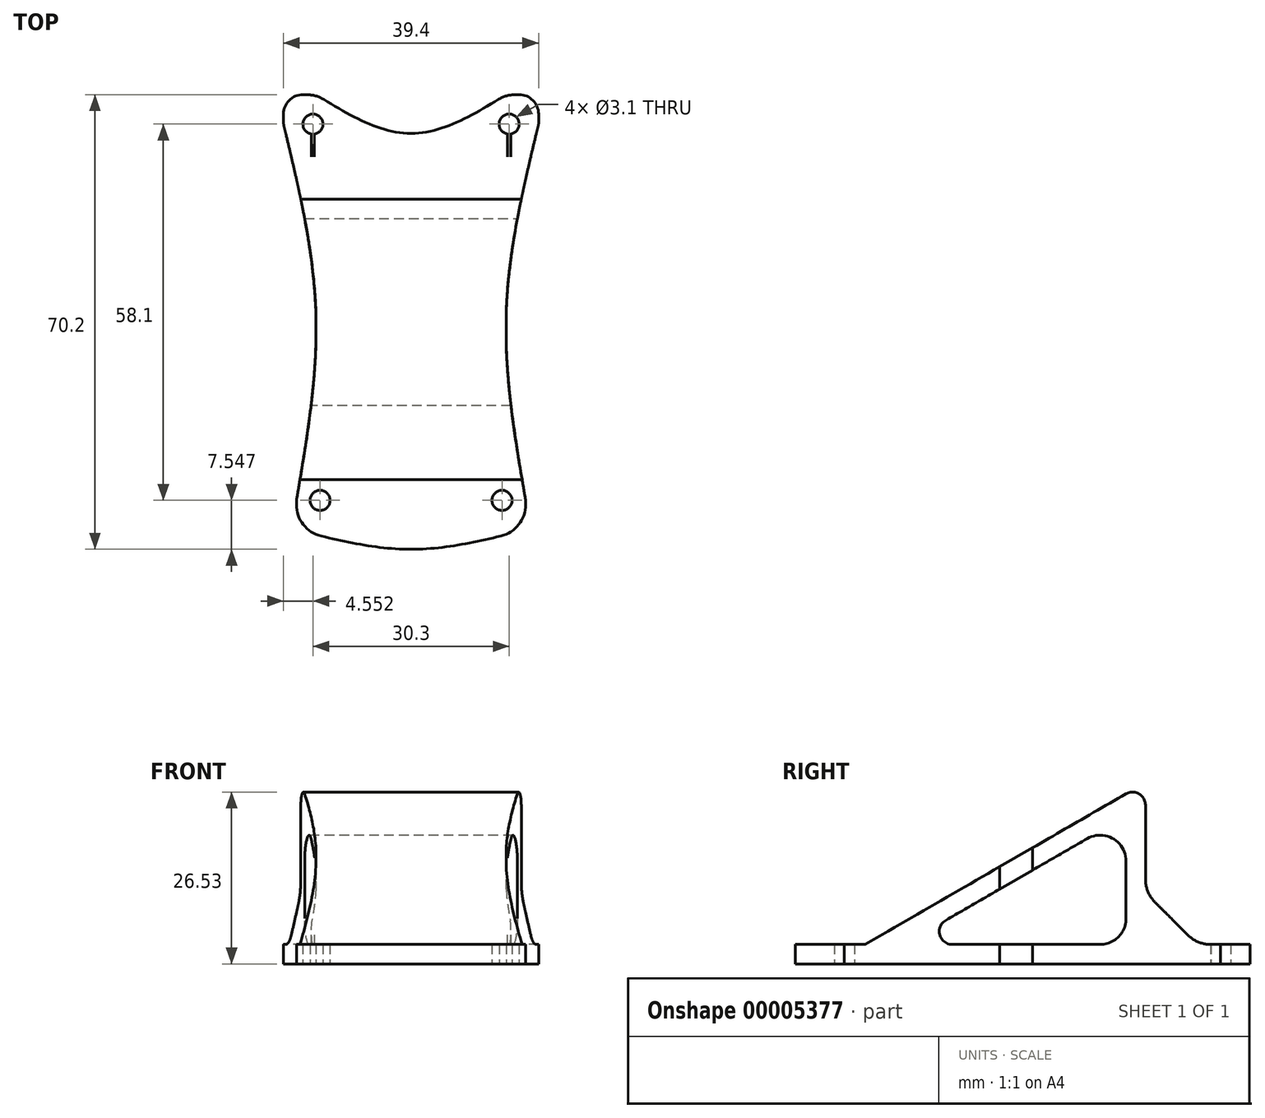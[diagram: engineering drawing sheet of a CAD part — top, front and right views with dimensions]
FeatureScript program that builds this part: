
annotation { "Feature Type Name" : "Feature", "Feature Type Description" : "" }
export const myFeature = defineFeature(function(context is Context, id is Id, definition is map)
    precondition{}
    {
        {
            var Q0;
            Q0=qCreatedBy(makeId("Top.planeOp"),FACE);
            var sketch = newSketch(context, id + "F0", { "sketchPlane" : qUnion([Q0])});
            skCircle(sketch, "E0", {"center": v(-54.15, 55.54) * mm, "radius": 1.55 * mm});
            skCircle(sketch, "E1", {"center": v(-23.85, 55.54) * mm, "radius": 1.55 * mm});
            skLineSegment(sketch, "E2.bottom", {"start": v(-58.7, 60.09) * mm, "end": v(-19.3, 60.09) * mm});
            skLineSegment(sketch, "E2.top", {"start": v(-58.7, -7.11) * mm, "end": v(-19.3, -7.11) * mm});
            skLineSegment(sketch, "E2.left", {"start": v(-58.7, 60.09) * mm, "end": v(-58.7, -7.11) * mm});
            skLineSegment(sketch, "E2.right", {"start": v(-19.3, 60.09) * mm, "end": v(-19.3, -7.11) * mm});
            skLineSegment(sketch, "E3", {"start": v(-19.3, 26.49) * mm, "end": v(-58.7, 26.49) * mm});
            skLineSegment(sketch, "E4", {"start": v(-39, 60.09) * mm, "end": v(-39, -7.11) * mm});
            skCircle(sketch, "E5", {"center": v(-24.95, -2.56) * mm, "radius": 1.55 * mm});
            skCircle(sketch, "E6", {"center": v(-53.05, -2.56) * mm, "radius": 1.55 * mm});
            skLineSegment(sketch, "E7", {"start": v(-56.7, -7.11) * mm, "end": v(-56.7, 60.09) * mm});
            skLineSegment(sketch, "E8", {"start": v(-53.7, 60.09) * mm, "end": v(-53.7, -7.11) * mm});
            skFitSpline(sketch, "E9", {"points": [v(-58.7, 55.54) * mm, v(-53.7, 26.49) * mm, v(-56.7, -2.56) * mm], "startDerivative": vector(13.98, -57.9) * mm, "endDerivative": vector(-10, -58.3) * mm});
            skLineSegment(sketch, "E10", {"start": v(-21.3, 60.09) * mm, "end": v(-21.3, -7.11) * mm});
            skLineSegment(sketch, "E11", {"start": v(-24.3, -7.11) * mm, "end": v(-24.3, 60.09) * mm});
            skFitSpline(sketch, "E12", {"points": [v(-19.3, 55.54) * mm, v(-24.3, 26.49) * mm, v(-21.3, -2.56) * mm], "startDerivative": vector(-13.98, -57.9) * mm, "endDerivative": vector(10, -58.3) * mm});
            skLineSegment(sketch, "E13", {"start": v(-58.7, -10.11) * mm, "end": v(-19.3, -10.11) * mm});
            skFitSpline(sketch, "E14", {"points": [v(-56.7, -7.11) * mm, v(-39, -10.11) * mm, v(-21.3, -7.11) * mm], "startDerivative": vector(35.4, -9) * mm, "endDerivative": vector(35.4, 9) * mm});
            skLineSegment(sketch, "E15", {"start": v(-44.39, 54.09) * mm, "end": v(-33.64, 54.09) * mm});
            skFitSpline(sketch, "E16", {"points": [v(-53.7, 60.09) * mm, v(-39, 54.09) * mm, v(-24.3, 60.09) * mm], "startDerivative": vector(29.4, -18) * mm, "endDerivative": vector(29.4, 18) * mm});
            skSolve(sketch);
        }
        {
            var Q0;
            Q0=makeQuery(id+"F0.imprint","IMPRINT",FACE,{"disambiguationData":[TD([[makeQuery(id+"F0.imprint","IMPRINT",EDGE,{"derivedFrom":sQuery(id+"F0.wireOp",EDGE,"E0")}),-1.0]])]});
            var Q1;
            Q1=makeQuery(id+"F0.imprint","IMPRINT",FACE,{"disambiguationData":[TD([[makeQuery(id+"F0.imprint","IMPRINT",EDGE,{"derivedFrom":sQuery(id+"F0.wireOp",EDGE,"E1")}),-1.0]])]});
            var Q2;
            Q2=makeQuery(id+"F0.imprint","IMPRINT",FACE,{"disambiguationData":[TD([[makeQuery(id+"F0.imprint","IMPRINT",EDGE,{"derivedFrom":sQuery(id+"F0.wireOp",EDGE,"e01dfe83-0717-4ae6-a988-163f855d4e40")}),-1.0]])]});
            var Q3;
            Q3=makeQuery(id+"F0.imprint","IMPRINT",FACE,{"disambiguationData":[TD([[makeQuery(id+"F0.imprint","IMPRINT",EDGE,{"derivedFrom":sQuery(id+"F0.wireOp",EDGE,"7627a010-1d8e-4650-84d9-1653207d3903")}),-1.0]])]});
            var Q4;
            {var subQ0=sQuery(id+"F0.wireOp",EDGE,"8a834bad-6aca-40db-864a-f019d0ae7b1d");Q4=makeQuery(id+"F0.imprint","IMPRINT",FACE,{"disambiguationData":[TD([[makeQuery(id+"F0.imprint","IMPRINT",EDGE,{"derivedFrom":subQ0}),1.0]])]});}
            var Q5;
            {var subQ7=sQuery(id+"F0.wireOp",EDGE,"E2.top");var subQ10=sQuery(id+"F0.wireOp",EDGE,"E4");var subQ12=makeQuery(id+"F0.imprint","INTERSECT",VERTEX,{"derivedFrom":[subQ7,subQ10]});Q5=makeQuery(id+"F0.imprint","IMPRINT",FACE,{"disambiguationData":[TD([[makeQuery(id+"F0.imprint","IMPRINT",EDGE,{"disambiguationData":[TD([[subQ12,1.0]])],"derivedFrom":subQ7}),1.0]])]});}
            var Q6;
            {var subQ1=sQuery(id+"F0.wireOp",EDGE,"E8");var subQ7=sQuery(id+"F0.wireOp",EDGE,"E0");var subQ8=makeQuery(id+"F0.imprint","INTERSECT",VERTEX,{"disambiguationData":[OD(0.0)],"derivedFrom":[subQ7,subQ1]});Q6=makeQuery(id+"F0.imprint","IMPRINT",FACE,{"disambiguationData":[TD([[makeQuery(id+"F0.imprint","IMPRINT",EDGE,{"disambiguationData":[TD([[subQ8,-1.0]])],"derivedFrom":subQ7}),-1.0]])]});}
            var Q7;
            {var subQ3=sQuery(id+"F0.wireOp",EDGE,"E2.left");var subQ5=sQuery(id+"F0.wireOp",EDGE,"E2.bottom");var subQ7=makeQuery(id+"F0.imprint","INTERSECT",VERTEX,{"derivedFrom":[subQ5,subQ3]});Q7=makeQuery(id+"F0.imprint","IMPRINT",FACE,{"disambiguationData":[TD([[makeQuery(id+"F0.imprint","IMPRINT",EDGE,{"disambiguationData":[TD([[subQ7,-1.0]])],"derivedFrom":subQ5}),-1.0]])]});}
            var Q8;
            {var subQ3=sQuery(id+"F0.wireOp",EDGE,"E7");var subQ8=sQuery(id+"F0.wireOp",EDGE,"E2.top");var subQ10=makeQuery(id+"F0.imprint","INTERSECT",VERTEX,{"derivedFrom":[subQ8,subQ3]});Q8=makeQuery(id+"F0.imprint","IMPRINT",FACE,{"disambiguationData":[TD([[makeQuery(id+"F0.imprint","IMPRINT",EDGE,{"disambiguationData":[TD([[subQ10,-1.0]])],"derivedFrom":subQ8}),1.0]])]});}
            var Q9;
            {var subQ3=sQuery(id+"F0.wireOp",EDGE,"E2.top");var subQ10=sQuery(id+"F0.wireOp",EDGE,"E4");var subQ12=makeQuery(id+"F0.imprint","INTERSECT",VERTEX,{"derivedFrom":[subQ3,subQ10]});Q9=makeQuery(id+"F0.imprint","IMPRINT",FACE,{"disambiguationData":[TD([[makeQuery(id+"F0.imprint","IMPRINT",EDGE,{"disambiguationData":[TD([[subQ12,-1.0]])],"derivedFrom":subQ3}),1.0]])]});}
            var Q10;
            {var subQ5=sQuery(id+"F0.wireOp",EDGE,"E10");var subQ8=sQuery(id+"F0.wireOp",EDGE,"E2.top");var subQ10=makeQuery(id+"F0.imprint","INTERSECT",VERTEX,{"derivedFrom":[subQ8,subQ5]});Q10=makeQuery(id+"F0.imprint","IMPRINT",FACE,{"disambiguationData":[TD([[makeQuery(id+"F0.imprint","IMPRINT",EDGE,{"disambiguationData":[TD([[subQ10,1.0]])],"derivedFrom":subQ8}),1.0]])]});}
            var Q11;
            {var subQ0=sQuery(id+"F0.wireOp",EDGE,"E11");var subQ3=sQuery(id+"F0.wireOp",EDGE,"E1");var subQ7=makeQuery(id+"F0.imprint","INTERSECT",VERTEX,{"disambiguationData":[OD(0.0)],"derivedFrom":[subQ3,subQ0]});Q11=makeQuery(id+"F0.imprint","IMPRINT",FACE,{"disambiguationData":[TD([[makeQuery(id+"F0.imprint","IMPRINT",EDGE,{"disambiguationData":[TD([[subQ7,-1.0]])],"derivedFrom":subQ3}),-1.0]])]});}
            var Q12;
            {var subQ3=sQuery(id+"F0.wireOp",EDGE,"E2.right");var subQ5=sQuery(id+"F0.wireOp",EDGE,"E2.bottom");var subQ7=makeQuery(id+"F0.imprint","INTERSECT",VERTEX,{"derivedFrom":[subQ5,subQ3]});Q12=makeQuery(id+"F0.imprint","IMPRINT",FACE,{"disambiguationData":[TD([[makeQuery(id+"F0.imprint","IMPRINT",EDGE,{"disambiguationData":[TD([[subQ7,1.0]])],"derivedFrom":subQ5}),-1.0]])]});}
            var Q13;
            {var subQ0=sQuery(id+"F0.wireOp",EDGE,"E2.top");var subQ4=makeQuery(id+"F0.imprint","INTERSECT",VERTEX,{"derivedFrom":[subQ0,sQuery(id+"F0.wireOp",EDGE,"E4")]});Q13=makeQuery(id+"F0.imprint","IMPRINT",FACE,{"disambiguationData":[TD([[makeQuery(id+"F0.imprint","IMPRINT",EDGE,{"disambiguationData":[TD([[subQ4,1.0]])],"derivedFrom":subQ0}),-1.0]])]});}
            var Q14;
            {var subQ2=sQuery(id+"F0.wireOp",EDGE,"E2.top");var subQ6=sQuery(id+"F0.wireOp",EDGE,"E2.right");var subQ8=makeQuery(id+"F0.imprint","INTERSECT",VERTEX,{"derivedFrom":[subQ2,subQ6]});Q14=makeQuery(id+"F0.imprint","IMPRINT",FACE,{"disambiguationData":[TD([[makeQuery(id+"F0.imprint","IMPRINT",EDGE,{"disambiguationData":[TD([[subQ8,1.0]])],"derivedFrom":subQ6}),-1.0]])]});}
            var Q15;
            {var subQ1=sQuery(id+"F0.wireOp",EDGE,"E3");var subQ3=sQuery(id+"F0.wireOp",EDGE,"E10");var subQ5=makeQuery(id+"F0.imprint","INTERSECT",VERTEX,{"derivedFrom":[subQ1,subQ3]});Q15=makeQuery(id+"F0.imprint","IMPRINT",FACE,{"disambiguationData":[TD([[makeQuery(id+"F0.imprint","IMPRINT",EDGE,{"disambiguationData":[TD([[subQ5,1.0]])],"derivedFrom":subQ3}),-1.0]])]});}
            var Q16;
            {var subQ3=sQuery(id+"F0.wireOp",EDGE,"E3");var subQ5=sQuery(id+"F0.wireOp",EDGE,"E2.right");var subQ6=makeQuery(id+"F0.imprint","INTERSECT",VERTEX,{"derivedFrom":[subQ5,subQ3]});Q16=makeQuery(id+"F0.imprint","IMPRINT",FACE,{"disambiguationData":[TD([[makeQuery(id+"F0.imprint","IMPRINT",EDGE,{"disambiguationData":[TD([[subQ6,1.0]])],"derivedFrom":subQ5}),-1.0]])]});}
            var Q17;
            {var subQ0=sQuery(id+"F0.wireOp",EDGE,"E12");var subQ3=sQuery(id+"F0.wireOp",EDGE,"E10");var subQ4=makeQuery(id+"F0.imprint","INTERSECT",VERTEX,{"disambiguationData":[OD(0.0)],"derivedFrom":[subQ3,subQ0]});Q17=makeQuery(id+"F0.imprint","IMPRINT",FACE,{"disambiguationData":[TD([[makeQuery(id+"F0.imprint","IMPRINT",EDGE,{"disambiguationData":[TD([[subQ4,1.0]])],"derivedFrom":subQ3}),-1.0]])]});}
            var Q18;
            {var subQ0=sQuery(id+"F0.wireOp",EDGE,"E12");var subQ1=sQuery(id+"F0.wireOp",EDGE,"E11");var subQ3=makeQuery(id+"F0.imprint","INTERSECT",VERTEX,{"derivedFrom":[subQ1,subQ0]});Q18=makeQuery(id+"F0.imprint","IMPRINT",FACE,{"disambiguationData":[TD([[makeQuery(id+"F0.imprint","IMPRINT",EDGE,{"disambiguationData":[TD([[subQ3,-1.0]])],"derivedFrom":subQ1}),1.0]])]});}
            extrude(context, id + "F1", {"entities" : qUnion([Q0, Q1, Q2, Q3, Q4, Q5, Q6, Q7, Q8, Q9, Q10, Q11, Q12, Q13, Q14, Q15, Q16, Q17, Q18]), "depth" : 3 * mm});
        }
        {
            var Q0;
            Q0=makeQuery(id+"F1.opExtrude","SWEPT_EDGE",EDGE,{"disambiguationData":[OSD([sQuery(id+"F0.wireOp",EDGE,"E2.bottom"),sQuery(id+"F0.wireOp",EDGE,"E2.left")])]});
            var Q1;
            Q1=makeQuery(id+"F1.opExtrude","SWEPT_EDGE",EDGE,{"disambiguationData":[OSD([sQuery(id+"F0.wireOp",EDGE,"E2.bottom"),sQuery(id+"F0.wireOp",EDGE,"E2.right")])]});
            var Q2;
            Q2=makeQuery(id+"F1.opExtrude","SWEPT_EDGE",EDGE,{"disambiguationData":[OSD([sQuery(id+"F0.wireOp",EDGE,"E2.top"),sQuery(id+"F0.wireOp",EDGE,"E2.left")])]});
            var Q3;
            Q3=makeQuery(id+"F1.opExtrude","SWEPT_EDGE",EDGE,{"disambiguationData":[OSD([sQuery(id+"F0.wireOp",EDGE,"E2.top"),sQuery(id+"F0.wireOp",EDGE,"E2.right")])]});
            fillet(context, id + "F2", {"entities" : qUnion([Q0, Q1, Q2, Q3]), "radius" : 3 * mm, "tangentPropagation" : true, "allowEdgeOverflow" : false});
        }
        {
            var Q0;
            Q0=makeQuery(id+"F1.opExtrude","SWEPT_EDGE",EDGE,{"disambiguationData":[OSD([sQuery(id+"F0.wireOp",EDGE,"E2.bottom"),sQuery(id+"F0.wireOp",EDGE,"E8"),sQuery(id+"F0.wireOp",EDGE,"E16")])]});
            var Q1;
            Q1=makeQuery(id+"F1.opExtrude","SWEPT_EDGE",EDGE,{"disambiguationData":[OSD([sQuery(id+"F0.wireOp",EDGE,"E2.bottom"),sQuery(id+"F0.wireOp",EDGE,"E11"),sQuery(id+"F0.wireOp",EDGE,"E16")])]});
            fillet(context, id + "F3", {"entities" : qUnion([Q0, Q1]), "radius" : 5 * mm, "tangentPropagation" : true, "allowEdgeOverflow" : false});
        }
        {
            var Q0;
            Q0=makeQuery(id+"F1.opExtrude","SWEPT_FACE",FACE,{"disambiguationData":[OSD([sQuery(id+"F0.wireOp",EDGE,"E2.right")])]});
            var sketch = newSketch(context, id + "F4", { "sketchPlane" : qUnion([Q0])});
            skLineSegment(sketch, "E17", {"start": v(0.63, 3) * mm, "end": v(43.93, 28) * mm});
            skLineSegment(sketch, "E18", {"start": v(43.93, 28) * mm, "end": v(43.93, 3) * mm});
            skLineSegment(sketch, "E19.0", {"start": v(40.93, 22.8) * mm, "end": v(40.93, 3) * mm});
            skLineSegment(sketch, "E19.1", {"start": v(2.13, 0.4) * mm, "end": v(40.93, 22.8) * mm});
            skSolve(sketch);
        }
        {
            var Q0;
            {var subQ6=sQuery(id+"F4.wireOp",EDGE,"E17");Q0=makeQuery(id+"F4.imprint","IMPRINT",FACE,{"disambiguationData":[TD([[makeQuery(id+"F4.imprint","IMPRINT",EDGE,{"derivedFrom":subQ6}),-1.0]])]});}
            extrude(context, id + "F5", {"entities" : qUnion([Q0]), "operationType" : NewBodyOperationType.ADD, "oppositeDirection" : true, "depth" : 39 * mm});
        }
        {
            var Q0;
            {var subQ0=sQuery(id+"F0.wireOp",EDGE,"E12");var subQ3=sQuery(id+"F0.wireOp",EDGE,"E10");var subQ4=makeQuery(id+"F0.imprint","INTERSECT",VERTEX,{"disambiguationData":[OD(0.0)],"derivedFrom":[subQ3,subQ0]});Q0=makeQuery(id+"F0.imprint","IMPRINT",FACE,{"disambiguationData":[TD([[makeQuery(id+"F0.imprint","IMPRINT",EDGE,{"disambiguationData":[TD([[subQ4,1.0]])],"derivedFrom":subQ3}),-1.0]])]});}
            var Q1;
            {var subQ2=sQuery(id+"F0.wireOp",EDGE,"E2.top");var subQ6=sQuery(id+"F0.wireOp",EDGE,"E2.right");var subQ8=makeQuery(id+"F0.imprint","INTERSECT",VERTEX,{"derivedFrom":[subQ2,subQ6]});Q1=makeQuery(id+"F0.imprint","IMPRINT",FACE,{"disambiguationData":[TD([[makeQuery(id+"F0.imprint","IMPRINT",EDGE,{"disambiguationData":[TD([[subQ8,1.0]])],"derivedFrom":subQ6}),-1.0]])]});}
            var Q2;
            {var subQ1=sQuery(id+"F0.wireOp",EDGE,"E3");var subQ3=sQuery(id+"F0.wireOp",EDGE,"E10");var subQ5=makeQuery(id+"F0.imprint","INTERSECT",VERTEX,{"derivedFrom":[subQ1,subQ3]});Q2=makeQuery(id+"F0.imprint","IMPRINT",FACE,{"disambiguationData":[TD([[makeQuery(id+"F0.imprint","IMPRINT",EDGE,{"disambiguationData":[TD([[subQ5,1.0]])],"derivedFrom":subQ3}),-1.0]])]});}
            var Q3;
            {var subQ3=sQuery(id+"F0.wireOp",EDGE,"E3");var subQ5=sQuery(id+"F0.wireOp",EDGE,"E2.right");var subQ6=makeQuery(id+"F0.imprint","INTERSECT",VERTEX,{"derivedFrom":[subQ5,subQ3]});Q3=makeQuery(id+"F0.imprint","IMPRINT",FACE,{"disambiguationData":[TD([[makeQuery(id+"F0.imprint","IMPRINT",EDGE,{"disambiguationData":[TD([[subQ6,1.0]])],"derivedFrom":subQ5}),-1.0]])]});}
            var Q4;
            {var subQ1=sQuery(id+"F0.wireOp",EDGE,"E3");var subQ3=sQuery(id+"F0.wireOp",EDGE,"E7");var subQ5=makeQuery(id+"F0.imprint","INTERSECT",VERTEX,{"derivedFrom":[subQ1,subQ3]});Q4=makeQuery(id+"F0.imprint","IMPRINT",FACE,{"disambiguationData":[TD([[makeQuery(id+"F0.imprint","IMPRINT",EDGE,{"disambiguationData":[TD([[subQ5,-1.0]])],"derivedFrom":subQ3}),-1.0]])]});}
            var Q5;
            {var subQ0=sQuery(id+"F0.wireOp",EDGE,"E7");var subQ3=sQuery(id+"F0.wireOp",EDGE,"E9");var subQ4=makeQuery(id+"F0.imprint","INTERSECT",VERTEX,{"disambiguationData":[OD(0.0)],"derivedFrom":[subQ0,subQ3]});Q5=makeQuery(id+"F0.imprint","IMPRINT",FACE,{"disambiguationData":[TD([[makeQuery(id+"F0.imprint","IMPRINT",EDGE,{"disambiguationData":[TD([[subQ4,-1.0]])],"derivedFrom":subQ0}),-1.0]])]});}
            var Q6;
            {var subQ4=sQuery(id+"F0.wireOp",EDGE,"E2.top");var subQ6=sQuery(id+"F0.wireOp",EDGE,"E2.left");var subQ8=makeQuery(id+"F0.imprint","INTERSECT",VERTEX,{"derivedFrom":[subQ4,subQ6]});Q6=makeQuery(id+"F0.imprint","IMPRINT",FACE,{"disambiguationData":[TD([[makeQuery(id+"F0.imprint","IMPRINT",EDGE,{"disambiguationData":[TD([[subQ8,1.0]])],"derivedFrom":subQ6}),1.0]])]});}
            var Q7;
            {var subQ3=sQuery(id+"F0.wireOp",EDGE,"E2.left");var subQ5=sQuery(id+"F0.wireOp",EDGE,"E3");var subQ7=makeQuery(id+"F0.imprint","INTERSECT",VERTEX,{"derivedFrom":[subQ3,subQ5]});Q7=makeQuery(id+"F0.imprint","IMPRINT",FACE,{"disambiguationData":[TD([[makeQuery(id+"F0.imprint","IMPRINT",EDGE,{"disambiguationData":[TD([[subQ7,1.0]])],"derivedFrom":subQ3}),1.0]])]});}
            extrude(context, id + "F6", {"entities" : qUnion([Q0, Q1, Q2, Q3, Q4, Q5, Q6, Q7]), "operationType" : NewBodyOperationType.REMOVE, "depth" : 35 * mm});
        }
        {
            var Q0;
            {var subQ0=sQuery(id+"F0.wireOp",EDGE,"E2.right");var subQ1=sQuery(id+"F4.wireOp",EDGE,"E18");Q0=makeQuery(id+"F5.boolean.opBoolean","SPLIT",EDGE,{"disambiguationData":[TD([makeQuery(id+"F1.opExtrude","SWEPT_FACE",FACE,{"disambiguationData":[OSD([subQ0])]})])],"derivedFrom":makeQuery(id+"F5.opExtrude","SWEPT_EDGE",EDGE,{"disambiguationData":[OSD([subQ0,subQ1])]})});}
            chamfer(context, id + "F7", {"entities" : qUnion([Q0]), "width" : 8 * mm, "tangentPropagation" : true});
        }
        {
            var Q0;
            Q0=makeQuery(id+"F1.opExtrude","SWEPT_EDGE",EDGE,{"disambiguationData":[OSD([sQuery(id+"F0.wireOp",EDGE,"E2.top"),sQuery(id+"F0.wireOp",EDGE,"E7"),sQuery(id+"F0.wireOp",EDGE,"E14")])]});
            var Q1;
            {var subQ0=sQuery(id+"F0.wireOp",EDGE,"E2.top");var subQ1=sQuery(id+"F0.wireOp",EDGE,"E14");Q1=makeQuery(id+"F6.boolean.opBoolean","MERGE",EDGE,{"derivedFrom":[makeQuery(id+"F2.opFillet","BLEND_EDGE",EDGE,{"blendedFrom":[makeQuery(id+"F1.opExtrude","SWEPT_EDGE",EDGE,{"disambiguationData":[OSD([subQ0,sQuery(id+"F0.wireOp",EDGE,"E2.right")])]}),makeQuery(id+"F1.opExtrude","SWEPT_FACE",FACE,{"disambiguationData":[OSD([subQ1])]})],"blendedInto":[makeQuery(id+"F1.opExtrude","SWEPT_FACE",FACE,{"disambiguationData":[OSD([subQ1])]})]}),makeQuery(id+"F6.opExtrude","SWEPT_EDGE",EDGE,{"disambiguationData":[OSD([subQ0,sQuery(id+"F0.wireOp",EDGE,"E10"),subQ1])]})]});}
            fillet(context, id + "F8", {"entities" : qUnion([Q0, Q1]), "radius" : 5 * mm, "tangentPropagation" : true, "allowEdgeOverflow" : false});
        }
        {
            var Q0;
            {var subQ0=sQuery(id+"F0.wireOp",EDGE,"E2.right");var subQ1=sQuery(id+"F4.wireOp",EDGE,"E19.1");Q0=makeQuery(id+"F5.boolean.opBoolean","SPLIT",EDGE,{"disambiguationData":[TD([makeQuery(id+"F1.opExtrude","SWEPT_FACE",FACE,{"disambiguationData":[OSD([subQ0])]})])],"derivedFrom":makeQuery(id+"F5.opExtrude","SWEPT_EDGE",EDGE,{"disambiguationData":[OSD([subQ0,subQ1])]})});}
            var Q1;
            Q1=makeQuery(id+"F5.opExtrude","SWEPT_EDGE",EDGE,{"disambiguationData":[OSD([sQuery(id+"F4.wireOp",EDGE,"E17"),sQuery(id+"F4.wireOp",EDGE,"E18")])]});
            var Q2;
            {var subQ0=sQuery(id+"F0.wireOp",EDGE,"E2.right");var subQ1=sQuery(id+"F4.wireOp",EDGE,"E17");Q2=makeQuery(id+"F5.boolean.opBoolean","SPLIT",EDGE,{"disambiguationData":[TD([makeQuery(id+"F1.opExtrude","SWEPT_FACE",FACE,{"disambiguationData":[OSD([subQ0])]})])],"derivedFrom":makeQuery(id+"F5.opExtrude","SWEPT_EDGE",EDGE,{"disambiguationData":[OSD([subQ0,subQ1])]})});}
            fillet(context, id + "F9", {"entities" : qUnion([Q0, Q1, Q2]), "radius" : 2 * mm, "tangentPropagation" : true, "allowEdgeOverflow" : false});
        }
        {
            var Q0;
            {var subQ0=sQuery(id+"F0.wireOp",EDGE,"E2.right");var subQ1=sQuery(id+"F4.wireOp",EDGE,"E19.0");Q0=makeQuery(id+"F5.boolean.opBoolean","SPLIT",EDGE,{"disambiguationData":[TD([makeQuery(id+"F1.opExtrude","SWEPT_FACE",FACE,{"disambiguationData":[OSD([subQ0])]})])],"derivedFrom":makeQuery(id+"F5.opExtrude","SWEPT_EDGE",EDGE,{"disambiguationData":[OSD([subQ0,subQ1])]})});}
            var Q1;
            Q1=makeQuery(id+"F5.opExtrude","SWEPT_EDGE",EDGE,{"disambiguationData":[OSD([sQuery(id+"F4.wireOp",EDGE,"E19.0"),sQuery(id+"F4.wireOp",EDGE,"E19.1")])]});
            fillet(context, id + "F10", {"entities" : qUnion([Q0, Q1]), "radius" : 4 * mm, "tangentPropagation" : true, "allowEdgeOverflow" : false});
        }
        {
            var Q0;
            {var subQ0=sQuery(id+"F0.wireOp",EDGE,"E2.right");var subQ1=sQuery(id+"F4.wireOp",EDGE,"E18");var subQ4=makeQuery(id+"F5.opExtrude","SWEPT_FACE",FACE,{"disambiguationData":[OSD([subQ1])]});Q0=makeQuery(id+"F7.opChamfer","BLEND_EDGE",EDGE,{"blendedFrom":[makeQuery(id+"F5.boolean.opBoolean","SPLIT",EDGE,{"disambiguationData":[TD([makeQuery(id+"F1.opExtrude","SWEPT_FACE",FACE,{"disambiguationData":[OSD([subQ0])]})])],"derivedFrom":makeQuery(id+"F5.opExtrude","SWEPT_EDGE",EDGE,{"disambiguationData":[OSD([subQ0,subQ1])]})}),subQ4],"blendedInto":[subQ4]});}
            var Q1;
            {var subQ0=sQuery(id+"F0.wireOp",EDGE,"E2.right");var subQ1=sQuery(id+"F4.wireOp",EDGE,"E18");var subQ7=sQuery(id+"F0.wireOp",EDGE,"E9");var subQ9=makeQuery(id+"F1.opExtrude","SWEPT_FACE",FACE,{"disambiguationData":[OSD([subQ0])]});var subQ10=sQuery(id+"F0.wireOp",EDGE,"E0");var subQ11=sQuery(id+"F0.wireOp",EDGE,"E1");var subQ12=sQuery(id+"F0.wireOp",EDGE,"E2.bottom");var subQ13=sQuery(id+"F0.wireOp",EDGE,"E2.left");var subQ14=sQuery(id+"F0.wireOp",EDGE,"E7");var subQ15=sQuery(id+"F0.wireOp",EDGE,"E16");var subQ16=makeQuery(id+"F1.opExtrude","CAP_FACE",FACE,{"disambiguationData":[OSD([subQ10,subQ11,subQ12,sQuery(id+"F0.wireOp",EDGE,"E2.top"),subQ13,subQ0,sQuery(id+"F0.wireOp",EDGE,"E5"),sQuery(id+"F0.wireOp",EDGE,"E6"),subQ14,subQ7,sQuery(id+"F0.wireOp",EDGE,"E14"),subQ15])],"isStart":false});Q1=makeQuery(id+"F7.opChamfer","BLEND_EDGE",EDGE,{"blendedFrom":[makeQuery(id+"F5.boolean.opBoolean","SPLIT",EDGE,{"disambiguationData":[TD([subQ9])],"derivedFrom":makeQuery(id+"F5.opExtrude","SWEPT_EDGE",EDGE,{"disambiguationData":[OSD([subQ0,subQ1])]})}),makeQuery(id+"F5.boolean.opBoolean","SPLIT",FACE,{"disambiguationData":[TD([makeQuery(id+"F1.opExtrude","SWEPT_FACE",FACE,{"disambiguationData":[OSD([subQ10])]})])],"derivedFrom":subQ16})],"blendedInto":[makeQuery(id+"F5.boolean.opBoolean","SPLIT",FACE,{"disambiguationData":[TD([makeQuery(id+"F1.opExtrude","SWEPT_FACE",FACE,{"disambiguationData":[OSD([subQ10])]})])],"derivedFrom":subQ16})]});}
            fillet(context, id + "F11", {"entities" : qUnion([Q0, Q1]), "radius" : 5 * mm, "tangentPropagation" : true, "allowEdgeOverflow" : false});
        }
    });
